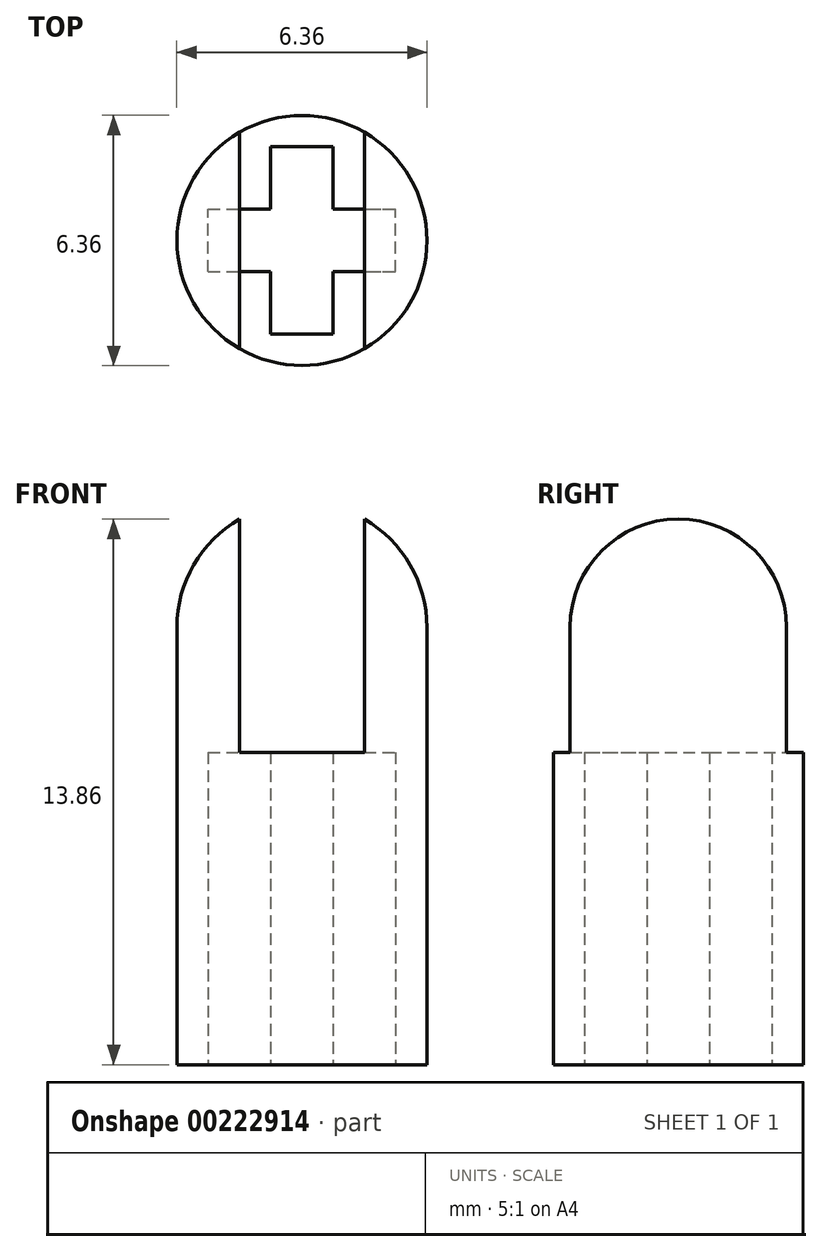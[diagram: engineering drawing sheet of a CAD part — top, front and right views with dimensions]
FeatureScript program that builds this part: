
annotation { "Feature Type Name" : "Feature", "Feature Type Description" : "" }
export const myFeature = defineFeature(function(context is Context, id is Id, definition is map)
    precondition{}
    {
        {
            var Q0;
            Q0=qCreatedBy(makeId("Top.planeOp"),FACE);
            var sketch = newSketch(context, id + "F0", { "sketchPlane" : qUnion([Q0])});
            skCircle(sketch, "E0", {"center": v(0, 0) * mm, "radius": 3.18 * mm});
            skSolve(sketch);
        }
        {
            var Q0;
            Q0 = qSketchRegion(id + "F0", true);
            extrude(context, id + "F1", {"entities" : qUnion([Q0]), "depth" : 14.29 * mm});
        }
        {
            var Q0;
            Q0=makeQuery(id+"F1.opExtrude","CAP_EDGE",EDGE,{"disambiguationData":[OSD([sQuery(id+"F0.wireOp",EDGE,"E0")])],"isStart":false});
            fillet(context, id + "F2", {"entities" : qUnion([Q0]), "radius" : 3.17 * mm, "tangentPropagation" : true, "allowEdgeOverflow" : false});
        }
        {
            var Q0;
            Q0=qCreatedBy(makeId("Front.planeOp"),FACE);
            var sketch = newSketch(context, id + "F3", { "sketchPlane" : qUnion([Q0])});
            skLineSegment(sketch, "E1", {"start": v(0, 0) * mm, "end": v(0, 7.94) * mm});
            skLineSegment(sketch, "E2", {"start": v(0, 7.94) * mm, "end": v(-1.59, 7.94) * mm});
            skLineSegment(sketch, "E3.MirrorCS", {"start": v(0, 7.94) * mm, "end": v(1.59, 7.94) * mm});
            skLineSegment(sketch, "E4.bottom", {"start": v(-1.59, 7.94) * mm, "end": v(1.59, 7.94) * mm});
            skLineSegment(sketch, "E4.top", {"start": v(-1.59, 14.9) * mm, "end": v(1.59, 14.9) * mm});
            skLineSegment(sketch, "E4.left", {"start": v(-1.59, 7.94) * mm, "end": v(-1.59, 14.9) * mm});
            skLineSegment(sketch, "E4.right", {"start": v(1.59, 7.94) * mm, "end": v(1.59, 14.9) * mm});
            skSolve(sketch);
        }
        {
            var Q0;
            Q0 = qSketchRegion(id + "F3", true);
            extrude(context, id + "F4", {"entities" : qUnion([Q0]), "operationType" : NewBodyOperationType.REMOVE, "endBound" : BoundingType.SYMMETRIC, "depth" : 25.4 * mm});
        }
        {
            var Q0;
            Q0=makeQuery(id+"F1.opExtrude","CAP_FACE",FACE,{"disambiguationData":[OSD([sQuery(id+"F0.wireOp",EDGE,"E0")])],"isStart":true});
            var sketch = newSketch(context, id + "F5", { "sketchPlane" : qUnion([Q0])});
            skLineSegment(sketch, "E5.bottom", {"start": v(-2.38, 0.8) * mm, "end": v(2.38, 0.8) * mm});
            skLineSegment(sketch, "E5.top", {"start": v(-2.38, -0.8) * mm, "end": v(2.38, -0.8) * mm});
            skLineSegment(sketch, "E5.left", {"start": v(-2.38, 0.8) * mm, "end": v(-2.38, -0.8) * mm});
            skLineSegment(sketch, "E5.right", {"start": v(2.38, 0.8) * mm, "end": v(2.38, -0.8) * mm});
            skPoint(sketch, "E5.middle", {"position": v(0, 0) * mm});
            skLineSegment(sketch, "E6.bottom", {"start": v(-0.8, 2.38) * mm, "end": v(0.8, 2.38) * mm});
            skLineSegment(sketch, "E6.top", {"start": v(-0.8, -2.38) * mm, "end": v(0.8, -2.38) * mm});
            skLineSegment(sketch, "E6.left", {"start": v(-0.8, 2.38) * mm, "end": v(-0.8, -2.38) * mm});
            skLineSegment(sketch, "E6.right", {"start": v(0.8, 2.38) * mm, "end": v(0.8, -2.38) * mm});
            skSolve(sketch);
        }
        {
            var Q0;
            Q0 = qSketchRegion(id + "F5", true);
            extrude(context, id + "F6", {"entities" : qUnion([Q0]), "operationType" : NewBodyOperationType.REMOVE, "oppositeDirection" : true, "depth" : 7.94 * mm});
        }
    });
